# Revit family: Glowica_natryskowa_wandaloodporna_slim
name_source: partatom
category: Osprzęt hydrauliczny
units: mm (PartAtom-declared; Revit-internal decimal feet)

## family parameters
Obiekt nadrzędny = Powierzchnia
Punkt obliczania pomieszczeń = Nie
Tnij formami wycięć po wczytaniu = Nie
Typ części = Normalny
Współdzielony = Nie
Wymiar okrągłego złącza = Użyj średnicy

## types (1)
- FAN6000S
    Depth / Glebokosc = 76 mm  [stored 0.249344 ft]
    Domyślna rzędna = 1219 mm
    Height / Wysokosc = 45 mm  [stored 0.147638 ft]
    Komentarze do typu = Głowica natryskowa wandaloodporna z regulacją nachylenia
    Manufacturer code / Kod producenta = 5901764296867
    Material finish / Wykonczenie = Mosiądz pokryty chromem
    Model = SLIM
    Opis = Głowica prysznicowa z przyłączem 1/2 cala jest najlepszym wyborem do natrysków w obiektach użytku publicznego. Niewielkie rozmiary wylewki prysznicowej oraz  jakość zastosowanych materiałów sprawia, że jest doskonałą armatura do natrysków w pływalniach, siłowniach, szatniach pracowniczych czy zakładach karnych.
    Producent = faneco.com
    Product code / Kod produktu = FAN6000S
    URL = https://faneco.com
    Weight / Waga = 0.46 kg
    Width / Szerokosc = 35 mm  [stored 0.114829 ft]

note: [stored X ft] marks values corroborated as IEEE doubles in the binary element streams (Revit-internal decimal feet)

## geometry (parser evidence)
native form markers: Sweep x6
no freeform markers — native parametric forms only
